# Revit family: TOTO_ツインデッキカウンター_ボウル一体タイプ(W500)_間口900mm_奥行450mm
name_source: partatom
category: 衛生器具
revit_build: Autodesk Revit 2018 (Build: 20190510_1515(x64)
units: mm (PartAtom-declared; Revit-internal decimal feet)

## family parameters
OmniClass タイトル = Sanitary, Laundry, and Cleaning Equipment
OmniClass 番号 = 23.45.00.00
パーツ タイプ = 標準
ロード時にボイドで切り取り = いいえ
丸型コネクタ寸法 = 直径を使用
作業面ベース = いいえ
共有 = いいえ
常に垂直 = はい
部屋計算ポイント = いいえ

## types (2) — shared parameters
BLCJ仕様バージョン = Version1.0
URL = https://jp.toto.com
メーカー型番 = MKWF PA14
付属品番 = REAH03B1S125A+TL347CU+RHE436-15+TLK06S01J+T6PM16+MFT3NB61
企業コード = 504845
使用水 = 上水
分類コード = 50301002100110
周 波 数 = 50/60Hz
品名 = ツインデッキカウンター
商品紹介URL = https://jp.toto.com
排水接続口情報 = 30鉛管｜R1 1/4 32A鋼管｜VP,VU40塩ビ管
最低使用圧力 = 0.1 MPa
最高使用圧力 = 0.8 MPa
極数 = 1
構成品番 = MKWFPA14+REAH03B1S125A+TL347CU+RHE436-15+TLK06S01J+T6PM16+MFT3NB61
汚水負荷単位 = 1
洗浄水量[L] = 0.0 L
流量（L/min） = 2.0 L/min
相 = 1
給水接続口 = 15  [stored 0.0492126 ft]
給水接続口情報 = R1/2
給水負荷単位(洗浄) = 2
製品出荷対象 = 国内
製造元 = TOTO株式会社
負荷分類 = コンセント
電    圧 = 100 V
zero-valued in all types: 上水負荷単位, 中水接続口, 中水負荷単位, 排水接続口, 排水芯・排水高さ, 標準取付高さ, 組合せフラグ, 給水負荷単位(水栓), 給湯負荷単位, 雑排水負荷単位, 電線管接続口

## per-type parameters (varying)
| type | あふれ面高さ | マテリアル/色情報 | モデル | 消費電力 |
| MKWF(750mm) | 750  [stored 2.46063 ft] | https://www.catalabo.org | MKWF | 604 W |
| MKWF(800mm) | 800  [stored 2.62467 ft] | パルフェウォームホワイト | MKWFPA14,REAH03B1S125A,TL347CU,RHE436-15,TLK06S01J,T6PM16,MFT3NB61 | 0 W |

note: [stored X ft] marks values corroborated as IEEE doubles in the binary element streams (Revit-internal decimal feet)
